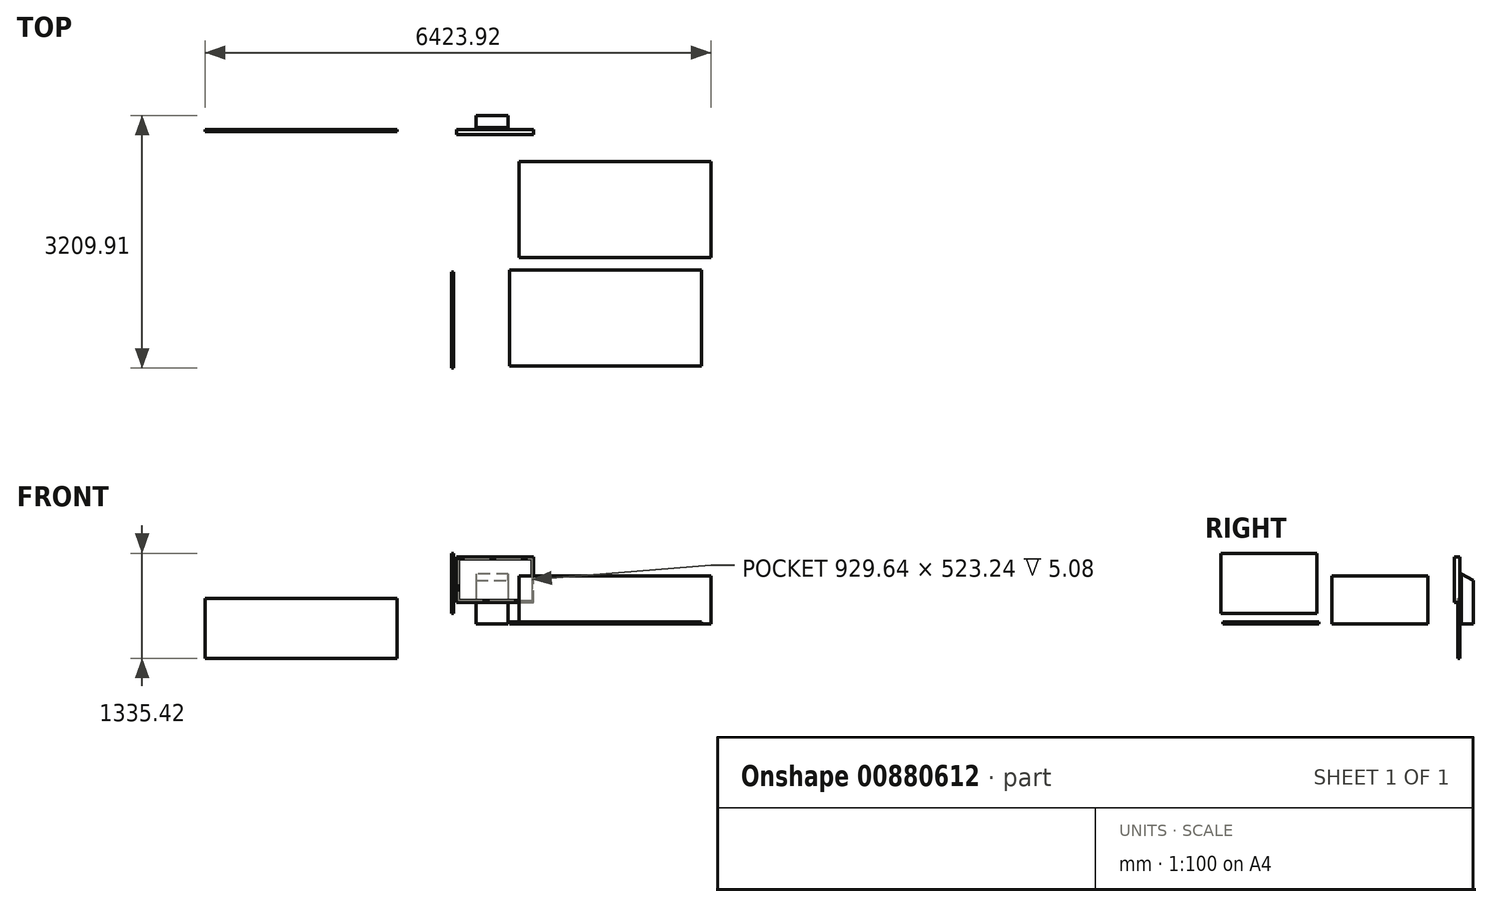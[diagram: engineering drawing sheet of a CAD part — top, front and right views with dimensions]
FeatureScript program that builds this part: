
annotation { "Feature Type Name" : "Feature", "Feature Type Description" : "" }
export const myFeature = defineFeature(function(context is Context, id is Id, definition is map)
    precondition{}
    {
        {
            var Q0;
            Q0=qCreatedBy(makeId("Top.planeOp"),FACE);
            var sketch = newSketch(context, id + "F0", { "sketchPlane" : qUnion([Q0])});
            skLineSegment(sketch, "E0.bottom", {"start": v(0, 0) * mm, "end": v(3657.6, 0) * mm});
            skLineSegment(sketch, "E0.top", {"start": v(0, -3048) * mm, "end": v(3657.6, -3048) * mm});
            skLineSegment(sketch, "E0.left", {"start": v(0, 0) * mm, "end": v(0, -3048) * mm});
            skLineSegment(sketch, "E0.right", {"start": v(3657.6, 0) * mm, "end": v(3657.6, -3048) * mm});
            skSolve(sketch);
        }
        {
            var Q0;
            Q0=qCreatedBy(makeId("Front.planeOp"),FACE);
            var sketch = newSketch(context, id + "F1", { "sketchPlane" : qUnion([Q0])});
            skLineSegment(sketch, "E1.bottom", {"start": v(65.64, 278.9) * mm, "end": v(1043.54, 278.9) * mm});
            skLineSegment(sketch, "E1.top", {"start": v(65.64, 852.93) * mm, "end": v(1043.54, 852.93) * mm});
            skLineSegment(sketch, "E1.left", {"start": v(65.64, 278.9) * mm, "end": v(65.64, 852.93) * mm});
            skLineSegment(sketch, "E1.right", {"start": v(1043.54, 278.9) * mm, "end": v(1043.54, 852.93) * mm});
            skSolve(sketch);
        }
        {
            var Q0;
            Q0 = qSketchRegion(id + "F1", true);
            extrude(context, id + "F2", {"entities" : qUnion([Q0]), "depth" : 66.04 * mm, "offsetDistance" : 25.4 * mm});
        }
        {
            var Q0;
            Q0=makeQuery(id+"F2.opExtrude","CAP_FACE",FACE,{"disambiguationData":[OSD([sQuery(id+"F1.wireOp",EDGE,"E1.bottom"),sQuery(id+"F1.wireOp",EDGE,"E1.top"),sQuery(id+"F1.wireOp",EDGE,"E1.left"),sQuery(id+"F1.wireOp",EDGE,"E1.right")])],"isStart":false});
            var sketch = newSketch(context, id + "F3", { "sketchPlane" : qUnion([Q0])});
            skLineSegment(sketch, "E2.bottom", {"start": v(89.77, 827.53) * mm, "end": v(1019.41, 827.53) * mm});
            skLineSegment(sketch, "E2.top", {"start": v(89.77, 304.3) * mm, "end": v(1019.41, 304.3) * mm});
            skLineSegment(sketch, "E2.left", {"start": v(89.77, 827.53) * mm, "end": v(89.77, 304.3) * mm});
            skLineSegment(sketch, "E2.right", {"start": v(1019.41, 827.53) * mm, "end": v(1019.41, 304.3) * mm});
            skLineSegment(sketch, "E3", {"start": v(65.64, 565.91) * mm, "end": v(1019.41, 565.91) * mm, "construction": true});
            skLineSegment(sketch, "E4", {"start": v(554.6, 278.9) * mm, "end": v(554.6, 304.3) * mm, "construction": true});
            skSolve(sketch);
        }
        {
            var Q0;
            Q0 = qSketchRegion(id + "F3", true);
            extrude(context, id + "F4", {"entities" : qUnion([Q0]), "operationType" : NewBodyOperationType.REMOVE, "oppositeDirection" : true, "depth" : 5.08 * mm, "offsetDistance" : 25.4 * mm});
        }
        {
            var Q0;
            Q0=makeQuery(id+"F0.imprint","IMPRINT",FACE,{"disambiguationData":[TD([[makeQuery(id+"F0.imprint","IMPRINT",EDGE,{"derivedFrom":sQuery(id+"F0.wireOp",EDGE,"E0.bottom")}),-1.0]])]});
            var sketch = newSketch(context, id + "F5", { "sketchPlane" : qUnion([Q0])});
            skLineSegment(sketch, "E5.bottom", {"start": v(855.55, -1625.66) * mm, "end": v(3293.95, -1625.66) * mm});
            skLineSegment(sketch, "E5.top", {"start": v(855.55, -406.46) * mm, "end": v(3293.95, -406.46) * mm});
            skLineSegment(sketch, "E5.left", {"start": v(855.55, -1625.66) * mm, "end": v(855.55, -406.46) * mm});
            skLineSegment(sketch, "E5.right", {"start": v(3293.95, -1625.66) * mm, "end": v(3293.95, -406.46) * mm});
            skSolve(sketch);
        }
        {
            var Q0;
            Q0 = qSketchRegion(id + "F5", true);
            extrude(context, id + "F6", {"entities" : qUnion([Q0]), "depth" : 609.6 * mm, "offsetDistance" : 25.4 * mm});
        }
        {
            var Q0;
            Q0=makeQuery(id+"F0.imprint","IMPRINT",FACE,{"disambiguationData":[TD([[makeQuery(id+"F0.imprint","IMPRINT",EDGE,{"derivedFrom":sQuery(id+"F0.wireOp",EDGE,"E0.bottom")}),-1.0]])]});
            var sketch = newSketch(context, id + "F7", { "sketchPlane" : qUnion([Q0])});
            skLineSegment(sketch, "E6.bottom", {"start": v(733.61, -1788.5) * mm, "end": v(3172.01, -1788.5) * mm});
            skLineSegment(sketch, "E6.top", {"start": v(733.61, -3007.7) * mm, "end": v(3172.01, -3007.7) * mm});
            skLineSegment(sketch, "E6.left", {"start": v(733.61, -1788.5) * mm, "end": v(733.61, -3007.7) * mm});
            skLineSegment(sketch, "E6.right", {"start": v(3172.01, -1788.5) * mm, "end": v(3172.01, -3007.7) * mm});
            skSolve(sketch);
        }
        {
            var Q0;
            Q0 = qSketchRegion(id + "F7", true);
            extrude(context, id + "F8", {"entities" : qUnion([Q0]), "depth" : 25.4 * mm, "offsetDistance" : 25.4 * mm});
        }
        {
            var Q0;
            Q0=qCreatedBy(makeId("Front.planeOp"),FACE);
            var sketch = newSketch(context, id + "F9", { "sketchPlane" : qUnion([Q0])});
            skLineSegment(sketch, "E7.bottom", {"start": v(-691.57, -434.44) * mm, "end": v(-3129.97, -434.44) * mm});
            skLineSegment(sketch, "E7.top", {"start": v(-691.57, 327.56) * mm, "end": v(-3129.97, 327.56) * mm});
            skLineSegment(sketch, "E7.left", {"start": v(-691.57, -434.44) * mm, "end": v(-691.57, 327.56) * mm});
            skLineSegment(sketch, "E7.right", {"start": v(-3129.97, -434.44) * mm, "end": v(-3129.97, 327.56) * mm});
            skSolve(sketch);
        }
        {
            var Q0;
            Q0 = qSketchRegion(id + "F9", true);
            extrude(context, id + "F10", {"entities" : qUnion([Q0]), "operationType" : NewBodyOperationType.ADD, "depth" : 25.4 * mm, "offsetDistance" : 25.4 * mm});
        }
        {
            var Q0;
            Q0=qCreatedBy(makeId("Right.planeOp"),FACE);
            var sketch = newSketch(context, id + "F11", { "sketchPlane" : qUnion([Q0])});
            skLineSegment(sketch, "E8.bottom", {"start": v(-1815.48, 138.98) * mm, "end": v(-3034.68, 138.98) * mm});
            skLineSegment(sketch, "E8.top", {"start": v(-1815.48, 900.98) * mm, "end": v(-3034.68, 900.98) * mm});
            skLineSegment(sketch, "E8.left", {"start": v(-1815.48, 138.98) * mm, "end": v(-1815.48, 900.98) * mm});
            skLineSegment(sketch, "E8.right", {"start": v(-3034.68, 138.98) * mm, "end": v(-3034.68, 900.98) * mm});
            skSolve(sketch);
        }
        {
            var Q0;
            Q0 = qSketchRegion(id + "F11", true);
            extrude(context, id + "F12", {"entities" : qUnion([Q0]), "depth" : 25.4 * mm, "offsetDistance" : 25.4 * mm});
        }
        {
            var Q0;
            Q0=makeQuery(id+"F0.imprint","IMPRINT",FACE,{"disambiguationData":[TD([[makeQuery(id+"F0.imprint","IMPRINT",EDGE,{"derivedFrom":sQuery(id+"F0.wireOp",EDGE,"E0.bottom")}),-1.0]])]});
            var sketch = newSketch(context, id + "F13", { "sketchPlane" : qUnion([Q0])});
            skLineSegment(sketch, "E9.bottom", {"start": v(717.9, 22.83) * mm, "end": v(311.5, 22.83) * mm});
            skLineSegment(sketch, "E9.top", {"start": v(717.9, 175.23) * mm, "end": v(311.5, 175.23) * mm});
            skLineSegment(sketch, "E9.left", {"start": v(717.9, 22.83) * mm, "end": v(717.9, 175.23) * mm});
            skLineSegment(sketch, "E9.right", {"start": v(311.5, 22.83) * mm, "end": v(311.5, 175.23) * mm});
            skSolve(sketch);
        }
        {
            var Q0;
            Q0 = qSketchRegion(id + "F13", true);
            extrude(context, id + "F14", {"entities" : qUnion([Q0]), "depth" : 640.08 * mm, "offsetDistance" : 25.4 * mm});
        }
        {
            var Q0;
            Q0=makeQuery(id+"F14.opExtrude","CAP_EDGE",EDGE,{"disambiguationData":[OSD([sQuery(id+"F13.wireOp",EDGE,"E9.top")])],"isStart":false});
            chamfer(context, id + "F15", {"entities" : qUnion([Q0]), "chamferType" : ChamferType.OFFSET_ANGLE, "width" : 152.4 * mm, "oppositeDirection" : false, "angle" : 30 * degree, "tangentPropagation" : true});
        }
    });
